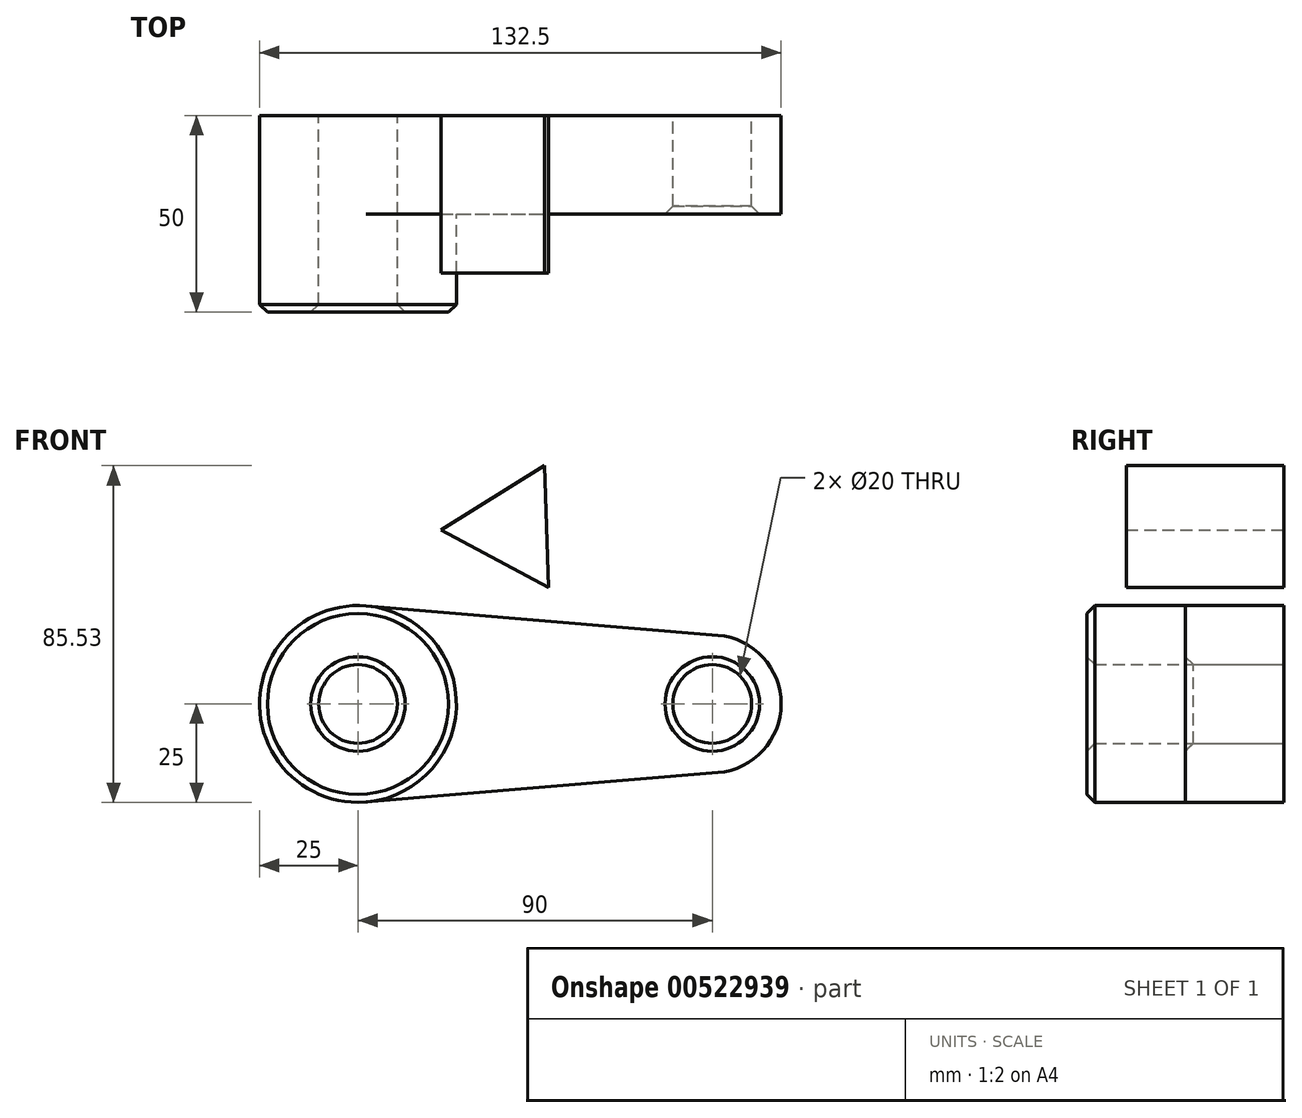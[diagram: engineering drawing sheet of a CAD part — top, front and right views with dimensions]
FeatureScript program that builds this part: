
annotation { "Feature Type Name" : "Feature", "Feature Type Description" : "" }
export const myFeature = defineFeature(function(context is Context, id is Id, definition is map)
    precondition{}
    {
        {
            var Q0;
            Q0=qCreatedBy(makeId("Front.planeOp"),FACE);
            var sketch = newSketch(context, id + "F0", { "sketchPlane" : qUnion([Q0])});
            skCircle(sketch, "E0", {"center": v(0, 0) * mm, "radius": 25 * mm});
            skCircle(sketch, "E1", {"center": v(90, 0) * mm, "radius": 17.5 * mm});
            skLineSegment(sketch, "E2", {"start": v(2.08, 24.91) * mm, "end": v(91.46, 17.44) * mm});
            skLineSegment(sketch, "E3", {"start": v(2.08, -24.91) * mm, "end": v(91.46, -17.44) * mm});
            skCircle(sketch, "E4", {"center": v(0, 0) * mm, "radius": 10 * mm});
            skCircle(sketch, "E5", {"center": v(90, 0) * mm, "radius": 10 * mm});
            skSolve(sketch);
        }
        {
            var Q0;
            Q0=qSketchRegion(id+"F0",true);
            extrude(context, id + "F1", {"entities" : qUnion([Q0]), "depth" : 25 * mm});
        }
        {
            var Q0;
            Q0=makeQuery(id+"F0.imprint","IMPRINT",FACE,{"disambiguationData":[TD([[makeQuery(id+"F0.imprint","IMPRINT",EDGE,{"derivedFrom":sQuery(id+"F0.wireOp",EDGE,"E4")}),-1.0]])]});
            extrude(context, id + "F2", {"entities" : qUnion([Q0]), "operationType" : NewBodyOperationType.ADD, "depth" : 50 * mm});
        }
        {
            var Q0;
            Q0=makeQuery(id+"F2.opExtrude","CAP_EDGE",EDGE,{"disambiguationData":[OSD([sQuery(id+"F0.wireOp",EDGE,"E0")])],"isStart":false});
            var Q1;
            Q1=makeQuery(id+"F2.opExtrude","CAP_EDGE",EDGE,{"disambiguationData":[OSD([sQuery(id+"F0.wireOp",EDGE,"E4")])],"isStart":false});
            var Q2;
            Q2=makeQuery(id+"F1.opExtrude","CAP_EDGE",EDGE,{"disambiguationData":[OSD([sQuery(id+"F0.wireOp",EDGE,"E5")])],"isStart":false});
            chamfer(context, id + "F3", {"entities" : qUnion([Q0, Q1, Q2]), "width" : 2 * mm, "tangentPropagation" : true});
        }
        {
            var Q0;
            Q0=qCreatedBy(makeId("Front.planeOp"),FACE);
            var sketch = newSketch(context, id + "F4", { "sketchPlane" : qUnion([Q0])});
            skCircle(sketch, "E6.cCircle", {"center": v(38.99, 44.77) * mm, "radius": 17.84 * mm, "construction": true});
            skLineSegment(sketch, "E6.0", {"start": v(48.45, 29.64) * mm, "end": v(21.16, 44.14) * mm});
            skLineSegment(sketch, "E6.1", {"start": v(21.16, 44.14) * mm, "end": v(47.36, 60.53) * mm});
            skLineSegment(sketch, "E6.2", {"start": v(47.36, 60.53) * mm, "end": v(48.45, 29.64) * mm});
            skSolve(sketch);
        }
        {
            var Q0;
            Q0=makeQuery(id+"F4.imprint","IMPRINT",FACE,{"disambiguationData":[TD([[makeQuery(id+"F4.imprint","IMPRINT",EDGE,{"derivedFrom":sQuery(id+"F4.wireOp",EDGE,"E6.0")}),-1.0]])]});
            extrude(context, id + "F5", {"entities" : qUnion([Q0]), "depth" : 40 * mm, "offsetDistance" : 25 * mm});
        }
    });
